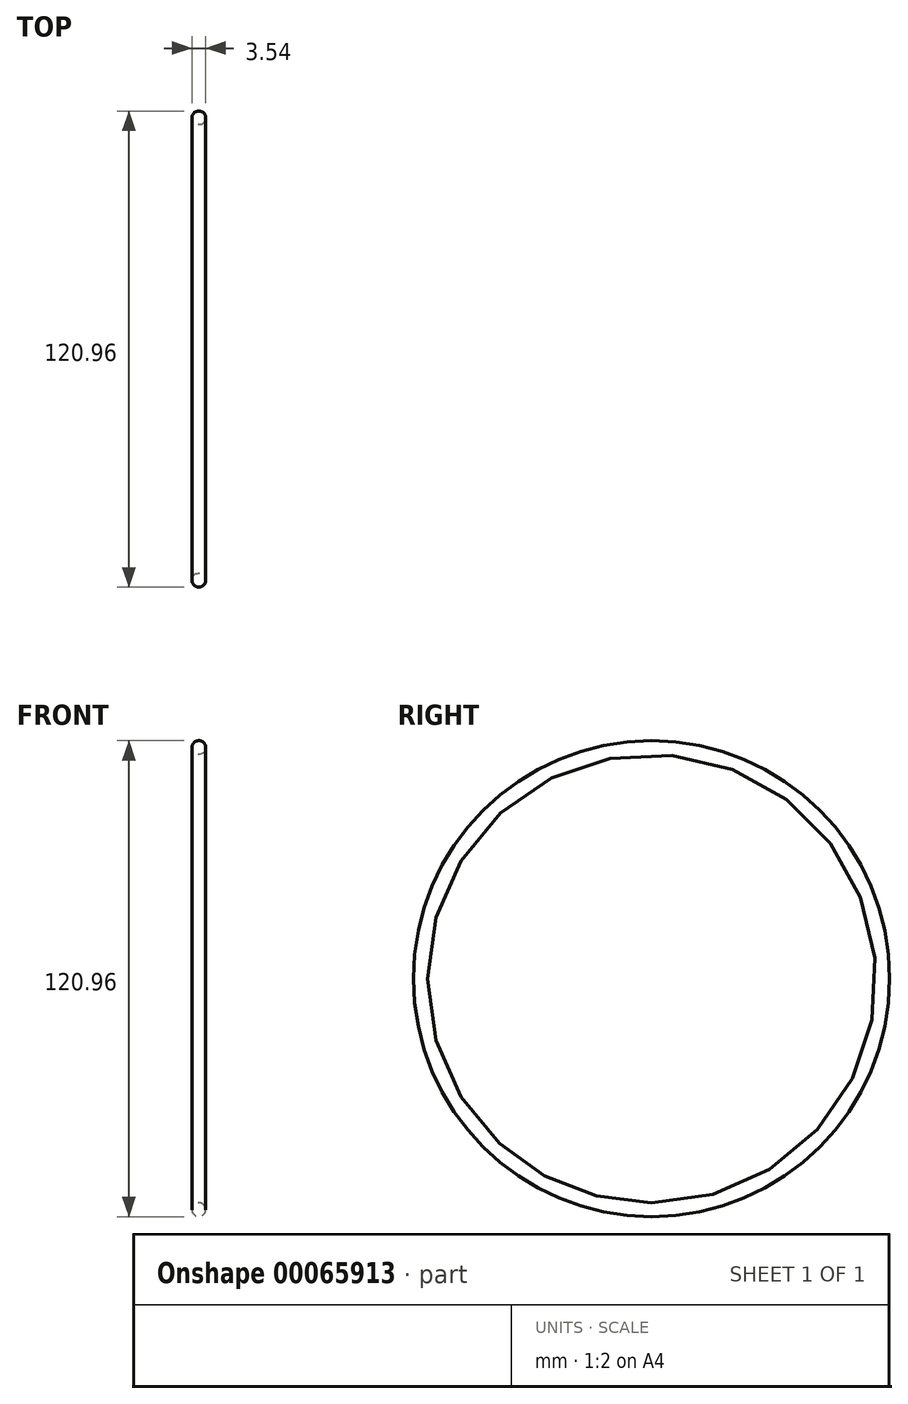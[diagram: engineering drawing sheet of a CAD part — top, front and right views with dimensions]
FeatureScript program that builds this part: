
annotation { "Feature Type Name" : "Feature", "Feature Type Description" : "" }
export const myFeature = defineFeature(function(context is Context, id is Id, definition is map)
    precondition{}
    {
        {
            var Q0;
            Q0=qCreatedBy(makeId("Front.planeOp"),FACE);
            var sketch = newSketch(context, id + "F0", { "sketchPlane" : qUnion([Q0])});
            skLineSegment(sketch, "E0", {"start": v(0, 0) * mm, "end": v(-6.06, 0) * mm, "construction": true});
            skCircle(sketch, "E1", {"center": v(0, 58.71) * mm, "radius": 1.77 * mm});
            skSolve(sketch);
        }
        {
            var Q0;
            Q0=makeQuery(id+"F0.imprint","IMPRINT",FACE,{"disambiguationData":[TD([[makeQuery(id+"F0.imprint","IMPRINT",EDGE,{"derivedFrom":sQuery(id+"F0.wireOp",EDGE,"E1")}),1.0]])]});
            var Q1;
            Q1=sQuery(id+"F0.wireOp",EDGE,"E0");
            revolve(context, id + "F1", {"entities" : qUnion([Q0]), "axis" : qUnion([Q1]), "revolveType" : RevolveType.FULL});
        }
    });
